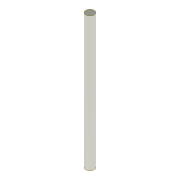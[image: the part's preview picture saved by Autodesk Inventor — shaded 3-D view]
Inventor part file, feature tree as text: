
AUTODESK INVENTOR PART (.ipt)
format: ipt  version: 2022 (Build 260153000, 153)  size: 74,240 bytes
history: native  units: mm
features: extrude x1, sketch x1
ambient origin geometry x8: Origin, YZ Plane, XZ Plane, XY Plane, X Axis, Y Axis, Z Axis, Center Point
bodies: Solid1 (feature_tree)
feature tree (2):
  extrude  "Extrusion1"  Depth=32.0mm TaperAngle=0.0deg
  sketch  "Sketch1"  dims[d0=2.0mm d1=32.0mm d2=0.0mm]
